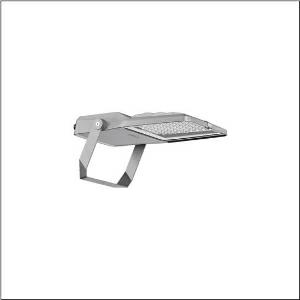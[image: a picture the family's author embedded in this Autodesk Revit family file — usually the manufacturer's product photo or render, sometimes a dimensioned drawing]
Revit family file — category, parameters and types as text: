
# Revit family: floodlight_fl_21_iq_mini___pl33t_5xa7772c3f1a_d349
name_source: partatom
category: Lighting Fixtures
units: mm (PartAtom-declared; Revit-internal decimal feet)

## family parameters
Cut with Voids When Loaded = No
Host = Face
Light Source = No
Part Type = Normal
Room Calculation Point = No
Round Connector Dimension = Use Diameter
Shared = No

## types (1)
- --- (1 x LED, 10390 lm, 87.2 W, 3000K)
    Apparent Load = 87 VA
    CIE Flux Codes = 26 75 99 100 100
    Color Rendering = 80
    Color Temperature = 3000K
    Default Elevation = 1800 mm
    Description = Floodlight FL 21 iQ mini, floodlight, primary light control with lens, of PMMA, primary optical cover: protective disc, of toughened safety glass, transparent, light distribution: PL33T, light emission: direct distribution, installation type: surface-mounted, LED, High Power LED, rated luminous flux: 10.390lm, luminous efficacy: 119lm/W, light colour: 830, colour temperature: 3000K, control gear: iQ Street-Remote/DALI, control: Street-Remote, Auto-Match, Temp-Guard, Night-Set, Smart-Wire, Desk-Remote (wireless, voltage-free reading and setting of iQ features in the workshop via application-optimized NFC function/RFID function), optimised constant luminous flux control (CLO 2.0), with terminal, 6-pole, mains connection: 220..240V, AC, 50/60Hz, start of lifetime: 87W, end of service life: 92W, reduction: 40W, luminaire housing, of diecast aluminium, powder-coated, Siteco® metallic grey (DB 702S), corrosivity category C5 mid according to DIN EN ISO 12944, suitable for swimming pools, chlorine-resistant, sealing non-destructively replaceable, mounting bracket, of steel, galvanised, powder-coated, Siteco® metallic grey (DB 702S), protection rating (complete): IP66, insulation class (complete): insulation class II (safety insulation), certification: CE, ENEC, VDE, protection symbol: D, impact resistance: IK08, permissible operating ambient temperature: -40..+40°C, permissible operating ambient temperature for outdoor applications: -40..+50°C, standard: DIN EN 12944, LABS conformity tested according to VDMA 24364:2018-05, packaging unit: 1 piece

Light Distribution: PL33T
    Height = 70 mm
    Lamp = 1 x LED
    Lamp Light Flux = 10390 lm
    Lamp Power = 87.2 W
    Lamp count = 1
    Length = 485 mm
    Luminous efficacy = 119 lm/W
    Manufacturer = Siteco
    ModVariant = No
    Model = 5XA7772C3F1A
    Number of Poles = 1
    OnlyDefault = Yes
    Power Factor = 1
    Product Name = Floodlight FL 21 iQ mini | PL33T
    Product group = floodlight | pylon annexe
    ProductGroupID = 6200
    Protection Class = Protection class II
    Protection Degree = IP 66
    RLX_Detail_Level = 1
    RLX_Emergency_Light_Flux = 0 lm
    RLX_Emergency_Type = 0
    RLX_Emergency_Type_DB = No
    RlxData = <blob elided: 96285 chars, md5=b5117076>
    Socket = socket
    Standby Power = 0 W
    System Light Flux = 10390 lm
    System Power = 87 W
    Type Comments = factory setting: luminous flux: 100 % | dim-lin: 254 | 456 mA
    Type Image = l_1006845.jpg
    URL = http://relux.com
    VarID = @adj_149456
    Voltage = 0 V
    Weight = 0.00 kg
    Width = 337 mm

## geometry (parser evidence)
native form markers: Blend x4, Sweep x12
no freeform markers — native parametric forms only
